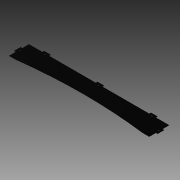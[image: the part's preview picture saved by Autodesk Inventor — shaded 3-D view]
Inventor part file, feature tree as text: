
AUTODESK INVENTOR PART (.ipt)
format: ipt  version: 2013 (Build 170138000, 138)  size: 153,088 bytes
history: native  units: mm
features: extrude x3, sketch x3, mirror x2
ambient origin geometry x8: Origin, YZ Plane, XZ Plane, XY Plane, X Axis, Y Axis, Z Axis, Center Point
bodies: Solid1 (feature_tree)
feature tree (8):
  extrude  "Extrusion1"  Depth=75.0mm
  mirror  "Mirror1"
  extrude  "Extrusion2"  Depth=6.477mm
  mirror  "Mirror2"
  extrude  "Extrusion3"  Depth=6.477mm TaperAngle=0.0deg
  sketch  "Sketch1"  dims[d0=525.0mm d2=75.0mm]
  sketch  "Sketch2"  dims[d3=25.0mm d4=6.477mm]
  sketch  "Sketch3"  dims[d5=50.0mm d6=6.477mm d7=0.0mm d8=4.0mm d10=1.5mm d11=2.5mm d13=2.5mm d14=10.0mm d15=0.0mm d16=25.0mm d17=15.0mm d18=10.0mm d19=0.0mm]
